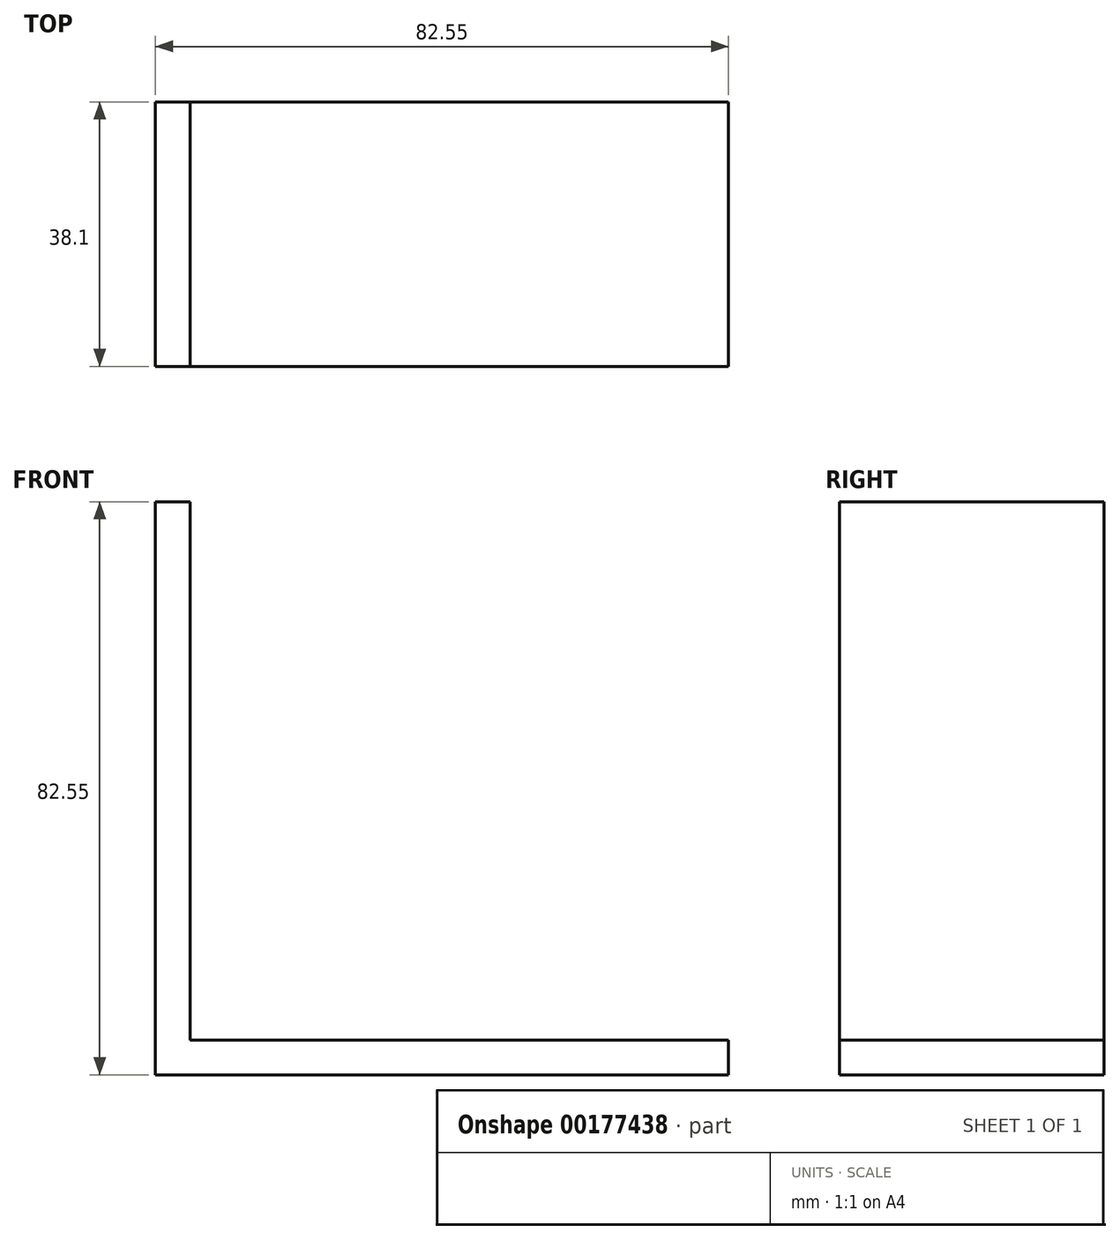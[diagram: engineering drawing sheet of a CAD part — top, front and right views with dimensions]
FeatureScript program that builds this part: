
annotation { "Feature Type Name" : "Feature", "Feature Type Description" : "" }
export const myFeature = defineFeature(function(context is Context, id is Id, definition is map)
    precondition{}
    {
        {
            var Q0;
            Q0=qCreatedBy(makeId("Front.planeOp"),FACE);
            var sketch = newSketch(context, id + "F0", { "sketchPlane" : qUnion([Q0])});
            skLineSegment(sketch, "E0", {"start": v(0, 0) * mm, "end": v(82.55, 0) * mm});
            skLineSegment(sketch, "E1", {"start": v(0, 0) * mm, "end": v(0, 82.55) * mm});
            skLineSegment(sketch, "E2.0", {"start": v(5, 5) * mm, "end": v(5, 82.55) * mm});
            skLineSegment(sketch, "E2.1", {"start": v(5, 5) * mm, "end": v(82.55, 5) * mm});
            skLineSegment(sketch, "E3", {"start": v(0, 82.55) * mm, "end": v(5, 82.55) * mm});
            skLineSegment(sketch, "E4", {"start": v(82.55, 0) * mm, "end": v(82.55, 5) * mm});
            skSolve(sketch);
        }
        {
            var Q0;
            Q0=makeQuery(id+"F0.imprint","IMPRINT",FACE,{"disambiguationData":[TD([[makeQuery(id+"F0.imprint","IMPRINT",EDGE,{"derivedFrom":sQuery(id+"F0.wireOp",EDGE,"E0")}),1.0]])]});
            extrude(context, id + "F1", {"entities" : qUnion([Q0]), "depth" : 38.1 * mm});
        }
    });
